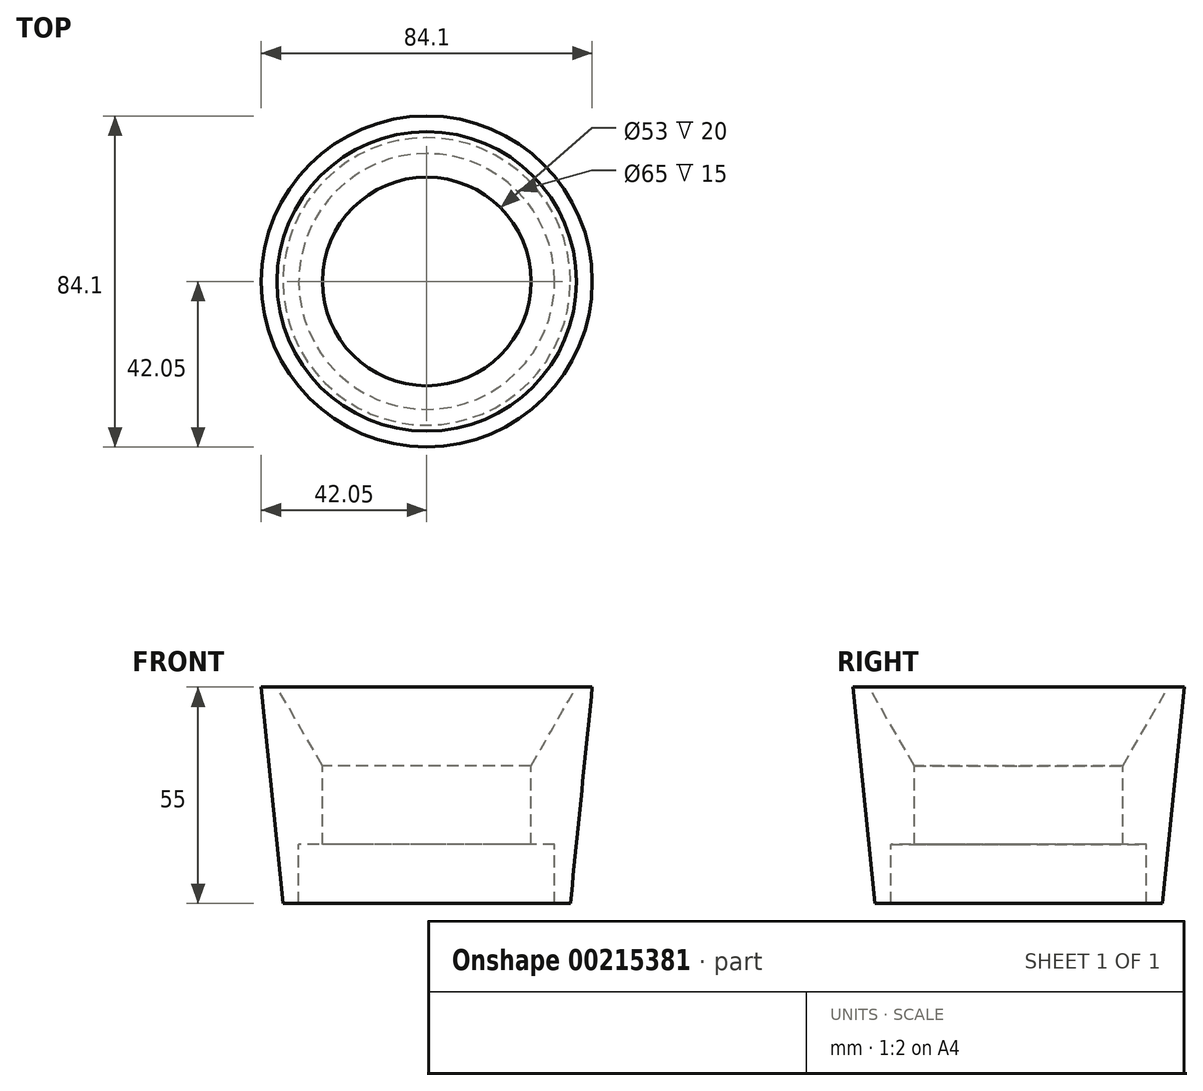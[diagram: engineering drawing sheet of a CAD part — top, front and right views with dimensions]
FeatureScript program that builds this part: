
annotation { "Feature Type Name" : "Feature", "Feature Type Description" : "" }
export const myFeature = defineFeature(function(context is Context, id is Id, definition is map)
    precondition{}
    {
        {
            var Q0;
            Q0=qCreatedBy(makeId("Front.planeOp"),FACE);
            var sketch = newSketch(context, id + "F0", { "sketchPlane" : qUnion([Q0])});
            skLineSegment(sketch, "E0", {"start": v(26.5, 0) * mm, "end": v(32.5, 0) * mm});
            skLineSegment(sketch, "E1", {"start": v(32.5, 0) * mm, "end": v(32.5, -15) * mm});
            skLineSegment(sketch, "E2", {"start": v(32.5, -15) * mm, "end": v(36.5, -15) * mm});
            skLineSegment(sketch, "E3", {"start": v(36.5, -15) * mm, "end": v(42.05, 40) * mm});
            skLineSegment(sketch, "E4", {"start": v(42.05, 40) * mm, "end": v(38.05, 40) * mm});
            skLineSegment(sketch, "E5", {"start": v(38.05, 40) * mm, "end": v(26.5, 20) * mm});
            skLineSegment(sketch, "E6", {"start": v(26.5, 20) * mm, "end": v(26.5, 0) * mm});
            skSolve(sketch);
        }
        {
            var Q0;
            Q0=qCreatedBy(makeId("Front.planeOp"),FACE);
            var sketch = newSketch(context, id + "F1", { "sketchPlane" : qUnion([Q0])});
            skLineSegment(sketch, "E7", {"start": v(0, 53.5) * mm, "end": v(0, 0) * mm});
            skSolve(sketch);
        }
        {
            var Q0;
            Q0=makeQuery(id+"F0.imprint","IMPRINT",FACE,{"disambiguationData":[TD([[makeQuery(id+"F0.imprint","IMPRINT",EDGE,{"derivedFrom":sQuery(id+"F0.wireOp",EDGE,"E0")}),1.0]])]});
            var Q1;
            Q1=sQuery(id+"F1.wireOp",EDGE,"E7");
            revolve(context, id + "F2", {"entities" : qUnion([Q0]), "axis" : qUnion([Q1]), "revolveType" : RevolveType.FULL});
        }
    });
